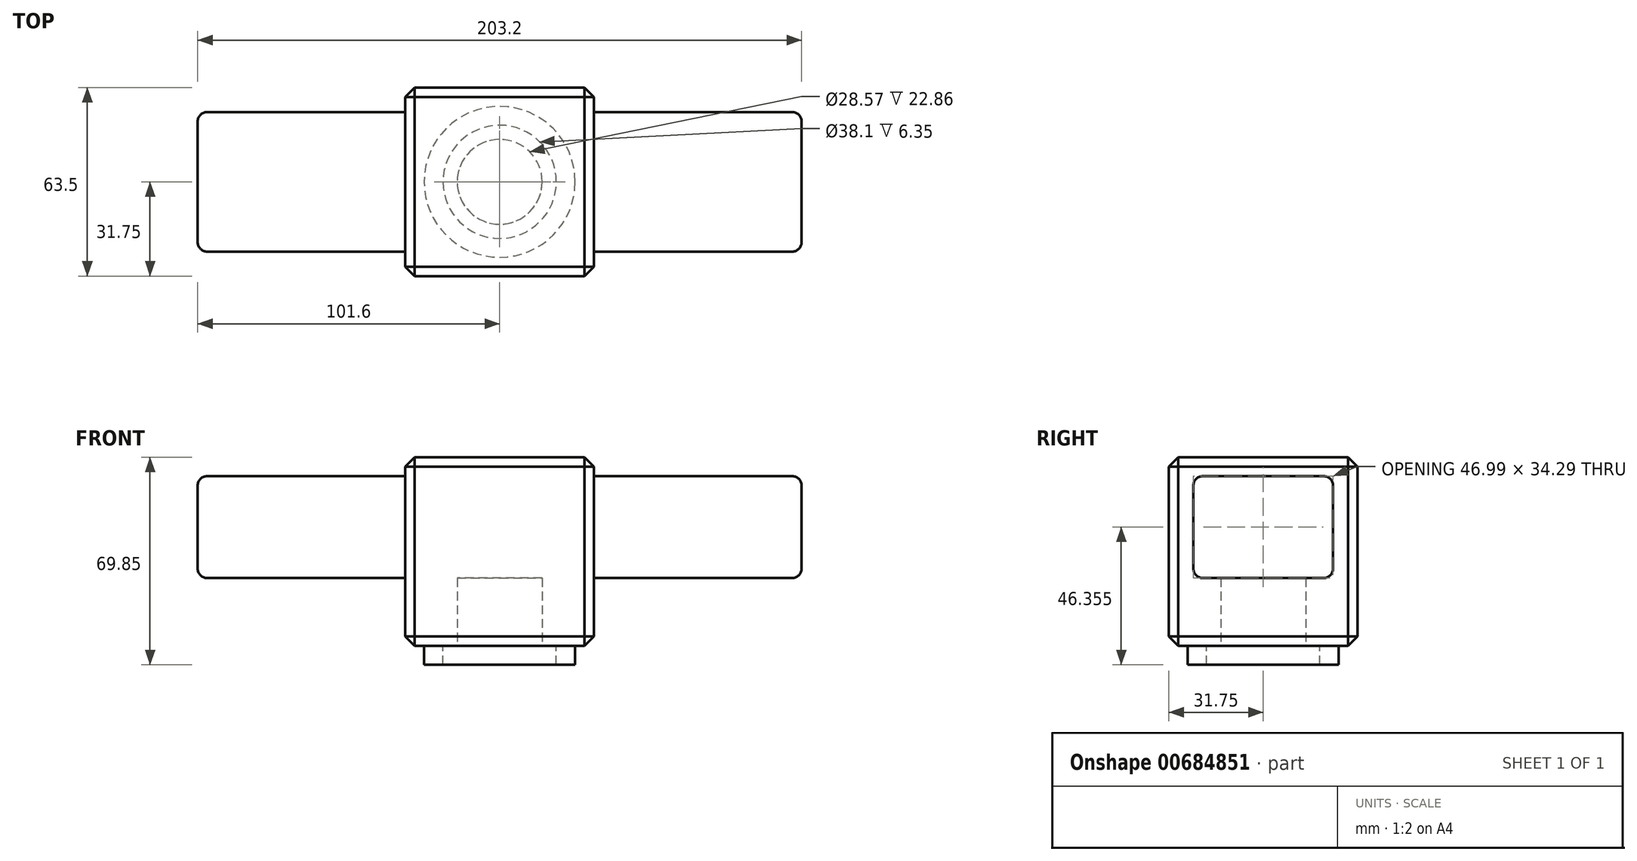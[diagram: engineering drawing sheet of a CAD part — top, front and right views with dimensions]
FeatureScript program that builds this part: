
annotation { "Feature Type Name" : "Feature", "Feature Type Description" : "" }
export const myFeature = defineFeature(function(context is Context, id is Id, definition is map)
    precondition{}
    {
        {
            var Q0;
            Q0=qCreatedBy(makeId("Top.planeOp"),FACE);
            var sketch = newSketch(context, id + "F0", { "sketchPlane" : qUnion([Q0])});
            skLineSegment(sketch, "E0.bottom", {"start": v(31.75, 31.75) * mm, "end": v(-31.75, 31.75) * mm});
            skLineSegment(sketch, "E0.top", {"start": v(31.75, -31.75) * mm, "end": v(-31.75, -31.75) * mm});
            skLineSegment(sketch, "E0.left", {"start": v(31.75, 31.75) * mm, "end": v(31.75, -31.75) * mm});
            skLineSegment(sketch, "E0.right", {"start": v(-31.75, 31.75) * mm, "end": v(-31.75, -31.75) * mm});
            skPoint(sketch, "E0.middle", {"position": v(0, 0) * mm});
            skSolve(sketch);
        }
        {
            var Q0;
            Q0=makeQuery(id+"F0.imprint","IMPRINT",FACE,{"disambiguationData":[TD([[makeQuery(id+"F0.imprint","IMPRINT",EDGE,{"derivedFrom":sQuery(id+"F0.wireOp",EDGE,"E0.bottom")}),1.0]])]});
            extrude(context, id + "F1", {"entities" : qUnion([Q0]), "depth" : 63.5 * mm, "offsetDistance" : 25.4 * mm});
        }
        {
            var Q0;
            Q0=qCreatedBy(makeId("Top.planeOp"),FACE);
            var sketch = newSketch(context, id + "F2", { "sketchPlane" : qUnion([Q0])});
            skCircle(sketch, "E1", {"center": v(0, 0) * mm, "radius": 25.4 * mm});
            skCircle(sketch, "E2", {"center": v(0, 0) * mm, "radius": 19.05 * mm});
            skCircle(sketch, "E3", {"center": v(0, 0) * mm, "radius": 14.29 * mm});
            skSolve(sketch);
        }
        {
            var Q0;
            Q0=makeQuery(id+"F2.imprint","IMPRINT",FACE,{"disambiguationData":[TD([[makeQuery(id+"F2.imprint","IMPRINT",EDGE,{"derivedFrom":sQuery(id+"F2.wireOp",EDGE,"E3")}),1.0]])]});
            var Q1;
            Q1=sQuery(id+"F2.wireOp",EDGE,"E3");
            extrude(context, id + "F3", {"entities" : qUnion([Q0]), "operationType" : NewBodyOperationType.REMOVE, "surfaceEntities" : qUnion([Q1]), "depth" : 50.8 * mm, "offsetDistance" : 25.4 * mm});
        }
        {
            var Q0;
            Q0 = qSketchRegion(id + "F2", true);
            extrude(context, id + "F4", {"entities" : qUnion([Q0]), "operationType" : NewBodyOperationType.ADD, "oppositeDirection" : true, "depth" : 6.35 * mm, "offsetDistance" : 25.4 * mm});
        }
        {
            var Q0;
            Q0=qCreatedBy(makeId("Right.planeOp"),FACE);
            var sketch = newSketch(context, id + "F5", { "sketchPlane" : qUnion([Q0])});
            skLineSegment(sketch, "E4.bottom", {"start": v(23.5, 57.15) * mm, "end": v(-23.5, 57.15) * mm});
            skLineSegment(sketch, "E4.top", {"start": v(23.5, 22.86) * mm, "end": v(-23.5, 22.86) * mm});
            skLineSegment(sketch, "E4.left", {"start": v(23.5, 57.15) * mm, "end": v(23.5, 22.86) * mm});
            skLineSegment(sketch, "E4.right", {"start": v(-23.5, 57.15) * mm, "end": v(-23.5, 22.86) * mm});
            skPoint(sketch, "E4.middle", {"position": v(0, 40) * mm});
            skSolve(sketch);
        }
        {
            var Q0;
            Q0 = qSketchRegion(id + "F5", true);
            extrude(context, id + "F6", {"entities" : qUnion([Q0]), "operationType" : NewBodyOperationType.ADD, "endBound" : BoundingType.SYMMETRIC, "depth" : 203.2 * mm, "offsetDistance" : 25.4 * mm});
        }
        {
            var Q0;
            Q0=makeQuery(id+"F1.opExtrude","SWEPT_FACE",FACE,{"disambiguationData":[OSD([sQuery(id+"F0.wireOp",EDGE,"E0.top")])]});
            var Q1;
            Q1=makeQuery(id+"F1.opExtrude","CAP_EDGE",EDGE,{"disambiguationData":[OSD([sQuery(id+"F0.wireOp",EDGE,"E0.left")])],"isStart":false});
            var Q2;
            Q2=makeQuery(id+"F1.opExtrude","CAP_EDGE",EDGE,{"disambiguationData":[OSD([sQuery(id+"F0.wireOp",EDGE,"E0.left")])],"isStart":true});
            var Q3;
            Q3=makeQuery(id+"F1.opExtrude","CAP_EDGE",EDGE,{"disambiguationData":[OSD([sQuery(id+"F0.wireOp",EDGE,"E0.right")])],"isStart":false});
            var Q4;
            Q4=makeQuery(id+"F1.opExtrude","CAP_EDGE",EDGE,{"disambiguationData":[OSD([sQuery(id+"F0.wireOp",EDGE,"E0.bottom")])],"isStart":false});
            var Q5;
            Q5=makeQuery(id+"F1.opExtrude","CAP_EDGE",EDGE,{"disambiguationData":[OSD([sQuery(id+"F0.wireOp",EDGE,"E0.right")])],"isStart":true});
            var Q6;
            Q6=makeQuery(id+"F1.opExtrude","CAP_EDGE",EDGE,{"disambiguationData":[OSD([sQuery(id+"F0.wireOp",EDGE,"E0.bottom")])],"isStart":true});
            var Q7;
            Q7=makeQuery(id+"F1.opExtrude","SWEPT_EDGE",EDGE,{"disambiguationData":[OSD([sQuery(id+"F0.wireOp",EDGE,"E0.bottom"),sQuery(id+"F0.wireOp",EDGE,"E0.right")])]});
            var Q8;
            Q8=makeQuery(id+"F1.opExtrude","SWEPT_EDGE",EDGE,{"disambiguationData":[OSD([sQuery(id+"F0.wireOp",EDGE,"E0.bottom"),sQuery(id+"F0.wireOp",EDGE,"E0.left")])]});
            chamfer(context, id + "F7", {"entities" : qUnion([Q0, Q1, Q2, Q3, Q4, Q5, Q6, Q7, Q8]), "width" : 3.17 * mm, "tangentPropagation" : true});
        }
        {
            var Q0;
            {var subQ0=sQuery(id+"F5.wireOp",EDGE,"E4.right");var subQ1=sQuery(id+"F5.wireOp",EDGE,"E4.bottom");Q0=makeQuery(id+"F6.boolean.opBoolean","SPLIT",EDGE,{"disambiguationData":[TD([makeQuery(id+"F1.opExtrude","SWEPT_FACE",FACE,{"disambiguationData":[OSD([sQuery(id+"F0.wireOp",EDGE,"E0.right")])]})])],"derivedFrom":makeQuery(id+"F6.opExtrude","SWEPT_EDGE",EDGE,{"disambiguationData":[OSD([subQ1,subQ0])]})});}
            var Q1;
            {var subQ0=sQuery(id+"F5.wireOp",EDGE,"E4.left");var subQ1=sQuery(id+"F5.wireOp",EDGE,"E4.bottom");Q1=makeQuery(id+"F6.boolean.opBoolean","SPLIT",EDGE,{"disambiguationData":[TD([makeQuery(id+"F1.opExtrude","SWEPT_FACE",FACE,{"disambiguationData":[OSD([sQuery(id+"F0.wireOp",EDGE,"E0.right")])]})])],"derivedFrom":makeQuery(id+"F6.opExtrude","SWEPT_EDGE",EDGE,{"disambiguationData":[OSD([subQ1,subQ0])]})});}
            var Q2;
            Q2=makeQuery(id+"F6.opExtrude","CAP_EDGE",EDGE,{"disambiguationData":[OSD([sQuery(id+"F5.wireOp",EDGE,"E4.bottom")])],"isStart":true});
            var Q3;
            Q3=makeQuery(id+"F6.opExtrude","CAP_EDGE",EDGE,{"disambiguationData":[OSD([sQuery(id+"F5.wireOp",EDGE,"E4.top")])],"isStart":true});
            var Q4;
            Q4=makeQuery(id+"F6.opExtrude","CAP_FACE",FACE,{"disambiguationData":[OSD([sQuery(id+"F5.wireOp",EDGE,"E4.bottom"),sQuery(id+"F5.wireOp",EDGE,"E4.top"),sQuery(id+"F5.wireOp",EDGE,"E4.left"),sQuery(id+"F5.wireOp",EDGE,"E4.right")])],"isStart":true});
            var Q5;
            Q5=makeQuery(id+"F6.opExtrude","CAP_EDGE",EDGE,{"disambiguationData":[OSD([sQuery(id+"F5.wireOp",EDGE,"E4.right")])],"isStart":true});
            var Q6;
            {var subQ0=sQuery(id+"F5.wireOp",EDGE,"E4.right");var subQ1=sQuery(id+"F5.wireOp",EDGE,"E4.top");Q6=makeQuery(id+"F6.boolean.opBoolean","SPLIT",EDGE,{"disambiguationData":[TD([makeQuery(id+"F1.opExtrude","SWEPT_FACE",FACE,{"disambiguationData":[OSD([sQuery(id+"F0.wireOp",EDGE,"E0.right")])]})])],"derivedFrom":makeQuery(id+"F6.opExtrude","SWEPT_EDGE",EDGE,{"disambiguationData":[OSD([subQ1,subQ0])]})});}
            var Q7;
            {var subQ0=sQuery(id+"F5.wireOp",EDGE,"E4.left");var subQ1=sQuery(id+"F5.wireOp",EDGE,"E4.top");Q7=makeQuery(id+"F6.boolean.opBoolean","SPLIT",EDGE,{"disambiguationData":[TD([makeQuery(id+"F1.opExtrude","SWEPT_FACE",FACE,{"disambiguationData":[OSD([sQuery(id+"F0.wireOp",EDGE,"E0.right")])]})])],"derivedFrom":makeQuery(id+"F6.opExtrude","SWEPT_EDGE",EDGE,{"disambiguationData":[OSD([subQ1,subQ0])]})});}
            var Q8;
            {var subQ0=sQuery(id+"F5.wireOp",EDGE,"E4.bottom");var subQ1=sQuery(id+"F5.wireOp",EDGE,"E4.left");Q8=makeQuery(id+"F6.boolean.opBoolean","SPLIT",EDGE,{"disambiguationData":[TD([makeQuery(id+"F1.opExtrude","SWEPT_FACE",FACE,{"disambiguationData":[OSD([sQuery(id+"F0.wireOp",EDGE,"E0.left")])]})])],"derivedFrom":makeQuery(id+"F6.opExtrude","SWEPT_EDGE",EDGE,{"disambiguationData":[OSD([subQ0,subQ1])]})});}
            var Q9;
            {var subQ0=sQuery(id+"F5.wireOp",EDGE,"E4.left");var subQ1=sQuery(id+"F5.wireOp",EDGE,"E4.top");Q9=makeQuery(id+"F6.boolean.opBoolean","SPLIT",EDGE,{"disambiguationData":[TD([makeQuery(id+"F1.opExtrude","SWEPT_FACE",FACE,{"disambiguationData":[OSD([sQuery(id+"F0.wireOp",EDGE,"E0.left")])]})])],"derivedFrom":makeQuery(id+"F6.opExtrude","SWEPT_EDGE",EDGE,{"disambiguationData":[OSD([subQ1,subQ0])]})});}
            var Q10;
            Q10=makeQuery(id+"F6.opExtrude","CAP_EDGE",EDGE,{"disambiguationData":[OSD([sQuery(id+"F5.wireOp",EDGE,"E4.left")])],"isStart":false});
            var Q11;
            Q11=makeQuery(id+"F6.opExtrude","CAP_EDGE",EDGE,{"disambiguationData":[OSD([sQuery(id+"F5.wireOp",EDGE,"E4.bottom")])],"isStart":false});
            var Q12;
            {var subQ0=sQuery(id+"F5.wireOp",EDGE,"E4.bottom");var subQ1=sQuery(id+"F5.wireOp",EDGE,"E4.right");Q12=makeQuery(id+"F6.boolean.opBoolean","SPLIT",EDGE,{"disambiguationData":[TD([makeQuery(id+"F1.opExtrude","SWEPT_FACE",FACE,{"disambiguationData":[OSD([sQuery(id+"F0.wireOp",EDGE,"E0.left")])]})])],"derivedFrom":makeQuery(id+"F6.opExtrude","SWEPT_EDGE",EDGE,{"disambiguationData":[OSD([subQ0,subQ1])]})});}
            var Q13;
            Q13=makeQuery(id+"F6.opExtrude","CAP_EDGE",EDGE,{"disambiguationData":[OSD([sQuery(id+"F5.wireOp",EDGE,"E4.top")])],"isStart":false});
            var Q14;
            Q14=makeQuery(id+"F6.opExtrude","CAP_EDGE",EDGE,{"disambiguationData":[OSD([sQuery(id+"F5.wireOp",EDGE,"E4.right")])],"isStart":false});
            var Q15;
            {var subQ0=sQuery(id+"F5.wireOp",EDGE,"E4.right");var subQ1=sQuery(id+"F5.wireOp",EDGE,"E4.top");Q15=makeQuery(id+"F6.boolean.opBoolean","SPLIT",EDGE,{"disambiguationData":[TD([makeQuery(id+"F1.opExtrude","SWEPT_FACE",FACE,{"disambiguationData":[OSD([sQuery(id+"F0.wireOp",EDGE,"E0.left")])]})])],"derivedFrom":makeQuery(id+"F6.opExtrude","SWEPT_EDGE",EDGE,{"disambiguationData":[OSD([subQ1,subQ0])]})});}
            fillet(context, id + "F8", {"entities" : qUnion([Q0, Q1, Q2, Q3, Q4, Q5, Q6, Q7, Q8, Q9, Q10, Q11, Q12, Q13, Q14, Q15]), "radius" : 3.17 * mm, "tangentPropagation" : true, "allowEdgeOverflow" : false});
        }
    });
